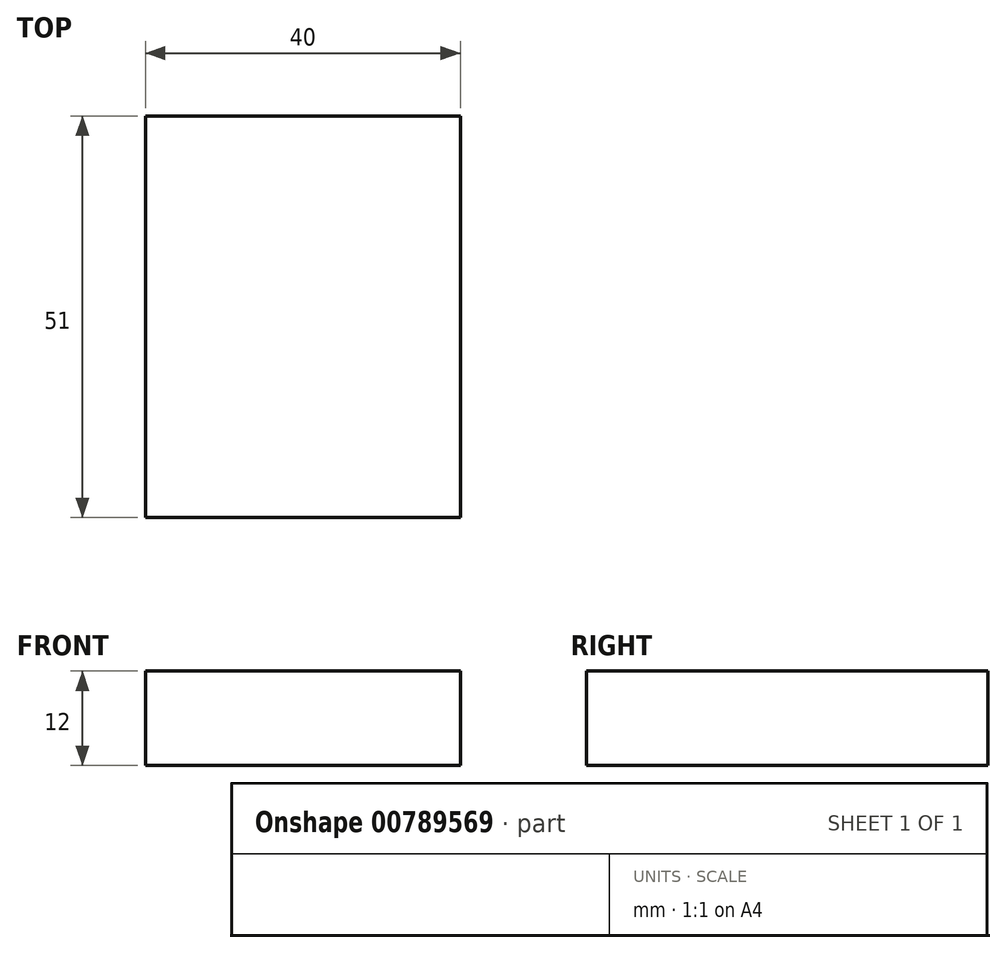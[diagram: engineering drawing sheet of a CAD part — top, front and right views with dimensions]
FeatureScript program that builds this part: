
annotation { "Feature Type Name" : "Feature", "Feature Type Description" : "" }
export const myFeature = defineFeature(function(context is Context, id is Id, definition is map)
    precondition{}
    {
        {
            var Q0;
            Q0=qCreatedBy(makeId("Front.planeOp"),FACE);
            var sketch = newSketch(context, id + "F0", { "sketchPlane" : qUnion([Q0])});
            skLineSegment(sketch, "E0.top", {"start": v(-34.97, 50.47) * mm, "end": v(-74.97, 50.47) * mm});
            skLineSegment(sketch, "E0.left", {"start": v(-34.97, 38.47) * mm, "end": v(-34.97, 50.47) * mm});
            skLineSegment(sketch, "E0.right", {"start": v(-74.97, 38.47) * mm, "end": v(-74.97, 50.47) * mm});
            skLineSegment(sketch, "E1", {"start": v(-74.97, 38.47) * mm, "end": v(-34.97, 38.47) * mm});
            skLineSegment(sketch, "E2.bottom", {"start": v(-74.5, -39.04) * mm, "end": v(-34.5, -39.04) * mm});
            skLineSegment(sketch, "E2.top", {"start": v(-74.5, -48.74) * mm, "end": v(-34.5, -48.74) * mm});
            skLineSegment(sketch, "E2.left", {"start": v(-74.5, -39.04) * mm, "end": v(-74.5, -48.74) * mm});
            skLineSegment(sketch, "E2.right", {"start": v(-34.5, -39.04) * mm, "end": v(-34.5, -48.74) * mm});
            skSolve(sketch);
        }
        {
            var Q0;
            Q0=makeQuery(id+"F0.imprint","IMPRINT",FACE,{"disambiguationData":[TD([[makeQuery(id+"F0.imprint","IMPRINT",EDGE,{"derivedFrom":sQuery(id+"F0.wireOp",EDGE,"E0.top")}),1.0]])]});
            var Q1;
            Q1=makeQuery(id+"F0.imprint","IMPRINT",FACE,{"disambiguationData":[TD([[makeQuery(id+"F0.imprint","IMPRINT",EDGE,{"derivedFrom":sQuery(id+"F0.wireOp",EDGE,"Oe4yk0z0-zHRJ-YtK5-qJxb-ESC1CReS1kv6.top")}),1.0]])]});
            extrude(context, id + "F1", {"entities" : qUnion([Q0, Q1]), "depth" : 51 * mm, "offsetDistance" : 25 * mm});
        }
    });
